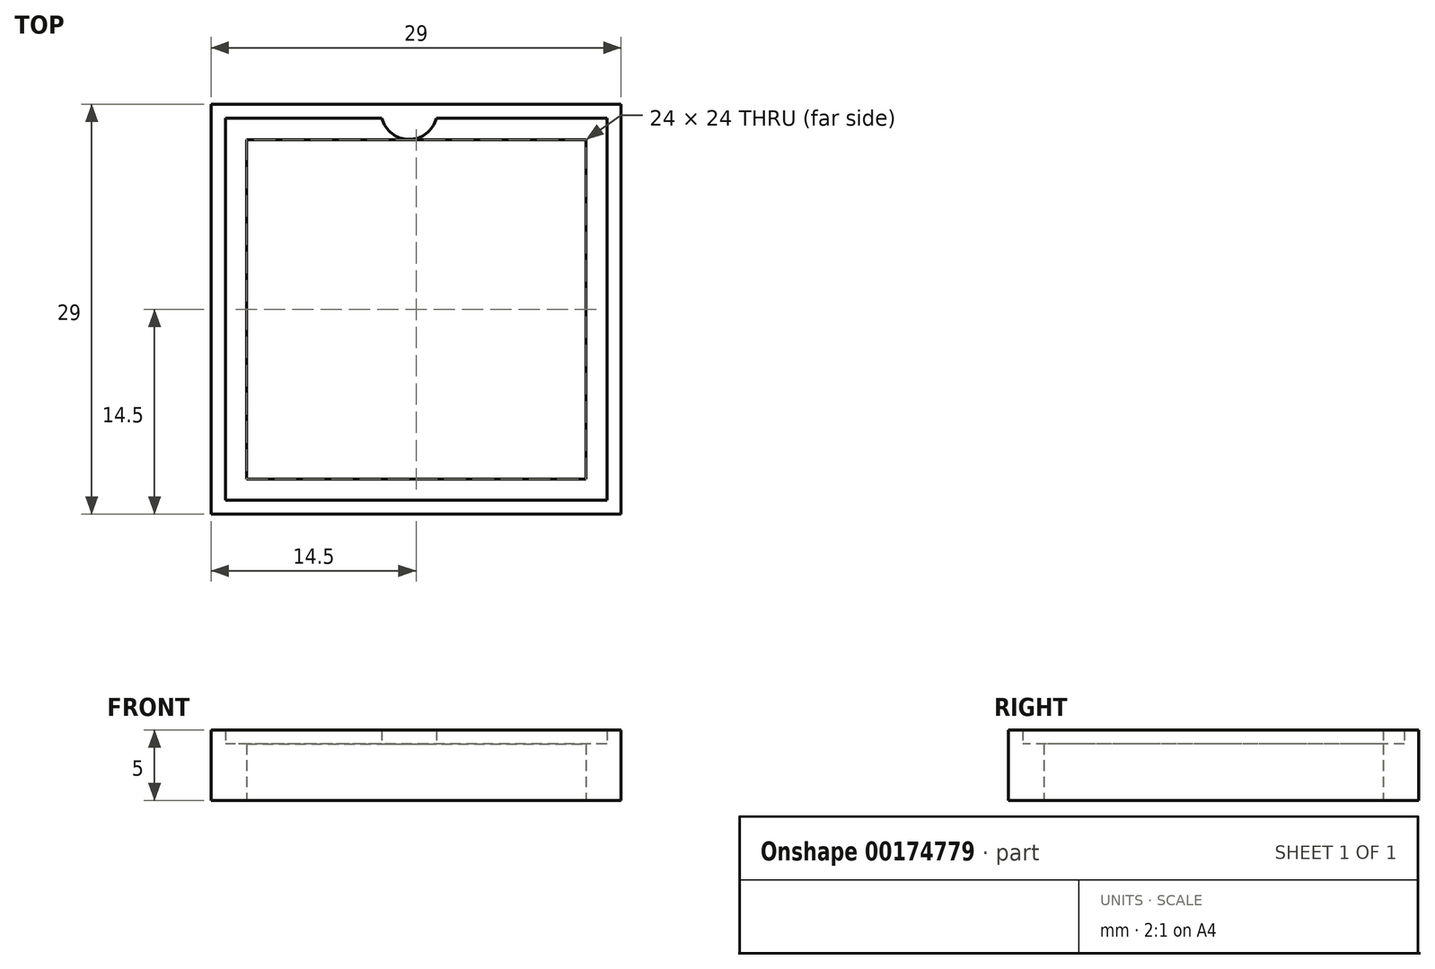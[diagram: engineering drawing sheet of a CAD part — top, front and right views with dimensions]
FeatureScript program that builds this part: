
annotation { "Feature Type Name" : "Feature", "Feature Type Description" : "" }
export const myFeature = defineFeature(function(context is Context, id is Id, definition is map)
    precondition{}
    {
        {
            var Q0;
            Q0=qCreatedBy(makeId("Top.planeOp"),FACE);
            var sketch = newSketch(context, id + "F0", { "sketchPlane" : qUnion([Q0])});
            skArc(sketch, "E0", {"start": v(11.57, 27.5) * mm, "mid": v(13.5, 26.01) * mm, "end": v(15.43, 27.5) * mm});
            skLineSegment(sketch, "E1", {"start": v(2, 26) * mm, "end": v(26, 26) * mm});
            skLineSegment(sketch, "E2", {"start": v(2, 26) * mm, "end": v(2, 2) * mm});
            skLineSegment(sketch, "E3", {"start": v(2, 2) * mm, "end": v(26, 2) * mm});
            skLineSegment(sketch, "E4", {"start": v(26, 2) * mm, "end": v(26, 26) * mm});
            skLineSegment(sketch, "E5.bottom", {"start": v(-0.5, -0.5) * mm, "end": v(28.5, -0.5) * mm});
            skLineSegment(sketch, "E5.top", {"start": v(-0.5, 28.5) * mm, "end": v(28.5, 28.5) * mm});
            skLineSegment(sketch, "E5.left", {"start": v(-0.5, -0.5) * mm, "end": v(-0.5, 28.5) * mm});
            skLineSegment(sketch, "E5.right", {"start": v(28.5, -0.5) * mm, "end": v(28.5, 28.5) * mm});
            skLineSegment(sketch, "E6.bottom", {"start": v(27.5, 27.5) * mm, "end": v(15.43, 27.5) * mm});
            skLineSegment(sketch, "E6.top", {"start": v(27.5, 0.5) * mm, "end": v(0.5, 0.5) * mm});
            skLineSegment(sketch, "E6.left", {"start": v(27.5, 27.5) * mm, "end": v(27.5, 0.5) * mm});
            skLineSegment(sketch, "E6.right", {"start": v(0.5, 27.5) * mm, "end": v(0.5, 0.5) * mm});
            skLineSegment(sketch, "E7.trimOffspring", {"start": v(11.57, 27.5) * mm, "end": v(0.5, 27.5) * mm});
            skSolve(sketch);
        }
        {
            var Q0;
            Q0=makeQuery(id+"F0.imprint","IMPRINT",FACE,{"disambiguationData":[TD([[makeQuery(id+"F0.imprint","IMPRINT",EDGE,{"derivedFrom":sQuery(id+"F0.wireOp",EDGE,"E0")}),1.0]])]});
            extrude(context, id + "F1", {"entities" : qUnion([Q0]), "depth" : 5 * mm});
        }
        {
            var Q0;
            Q0=makeQuery(id+"F0.imprint","IMPRINT",FACE,{"disambiguationData":[TD([[makeQuery(id+"F0.imprint","IMPRINT",EDGE,{"derivedFrom":sQuery(id+"F0.wireOp",EDGE,"E0")}),-1.0]])]});
            extrude(context, id + "F2", {"entities" : qUnion([Q0]), "operationType" : NewBodyOperationType.ADD, "depth" : 4 * mm});
        }
    });
